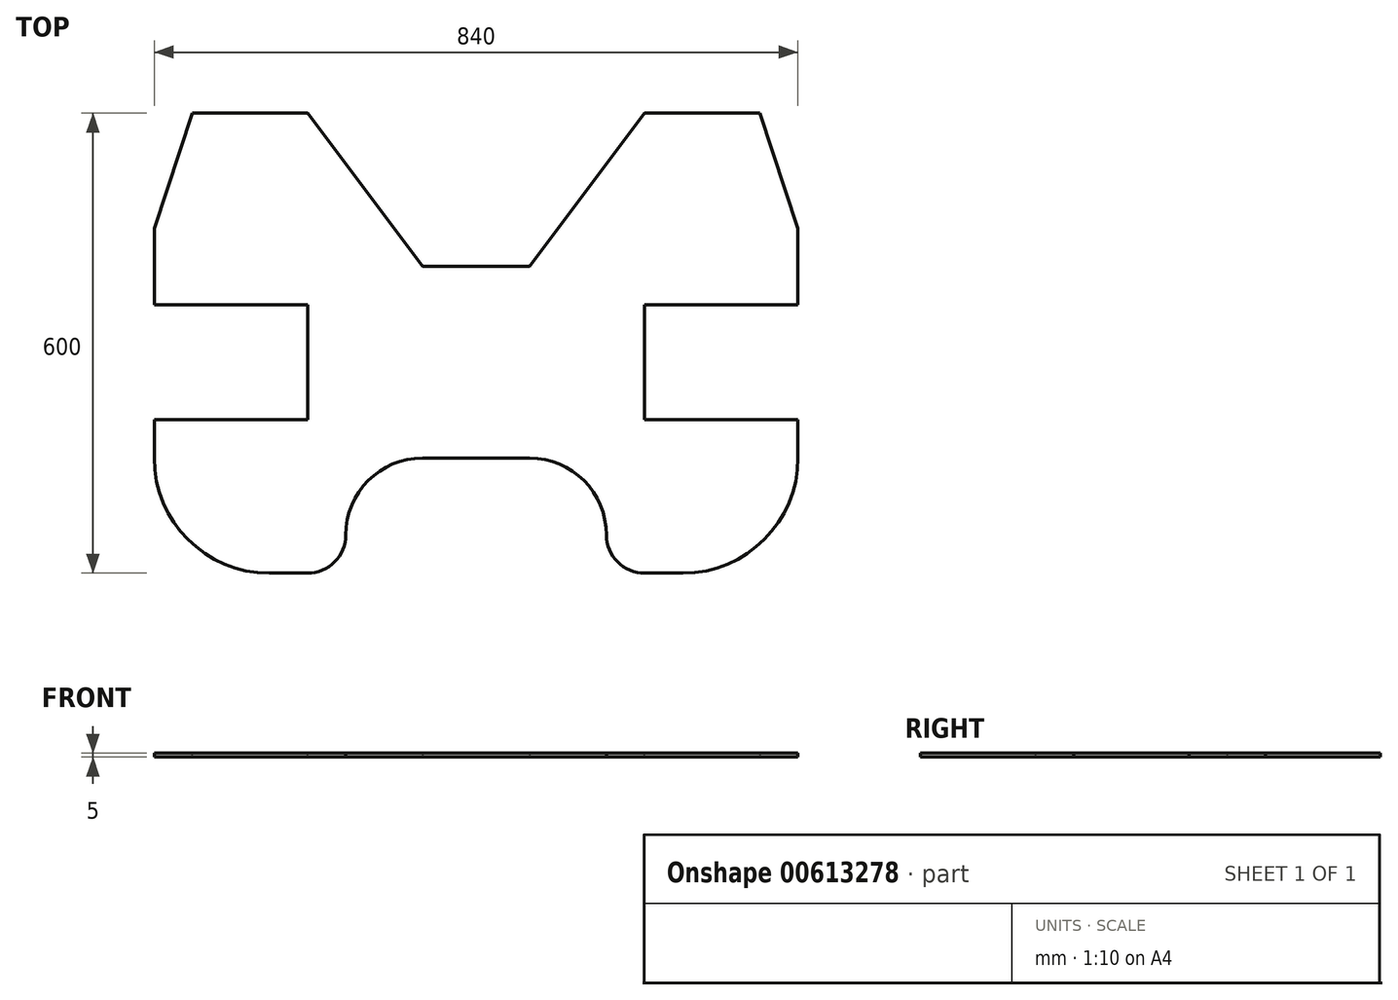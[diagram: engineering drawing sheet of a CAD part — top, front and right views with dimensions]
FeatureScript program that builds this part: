
annotation { "Feature Type Name" : "Feature", "Feature Type Description" : "" }
export const myFeature = defineFeature(function(context is Context, id is Id, definition is map)
    precondition{}
    {
        {
            var Q0;
            Q0=qCreatedBy(makeId("Top.planeOp"),FACE);
            var sketch = newSketch(context, id + "F0", { "sketchPlane" : qUnion([Q0])});
            skLineSegment(sketch, "E0.bottom", {"start": v(220, 125) * mm, "end": v(-220, 125) * mm});
            skLineSegment(sketch, "E0.top", {"start": v(220, -125) * mm, "end": v(-220, -125) * mm});
            skLineSegment(sketch, "E0.left", {"start": v(220, 125) * mm, "end": v(220, -125) * mm});
            skLineSegment(sketch, "E0.right", {"start": v(-220, 125) * mm, "end": v(-220, -125) * mm});
            skPoint(sketch, "E0.middle", {"position": v(0, 0) * mm});
            skSolve(sketch);
        }
        {
            var Q0;
            Q0 = qSketchRegion(id + "F0", true);
            extrude(context, id + "F1", {"entities" : qUnion([Q0]), "depth" : 5 * mm, "offsetDistance" : 25 * mm});
        }
        {
            var Q0;
            Q0=makeQuery(id+"F1.opExtrude","CAP_FACE",FACE,{"disambiguationData":[OSD([sQuery(id+"F0.wireOp",EDGE,"E0.bottom"),sQuery(id+"F0.wireOp",EDGE,"E0.top"),sQuery(id+"F0.wireOp",EDGE,"E0.left"),sQuery(id+"F0.wireOp",EDGE,"E0.right")])],"isStart":true});
            var sketch = newSketch(context, id + "F2", { "sketchPlane" : qUnion([Q0])});
            skLineSegment(sketch, "E1.bottom", {"start": v(-170, 75) * mm, "end": v(-420, 75) * mm});
            skLineSegment(sketch, "E1.top", {"start": v(-170, 275) * mm, "end": v(-420, 275) * mm});
            skLineSegment(sketch, "E1.left", {"start": v(-170, 75) * mm, "end": v(-170, 275) * mm});
            skLineSegment(sketch, "E1.right", {"start": v(-420, 75) * mm, "end": v(-420, 275) * mm});
            skLineSegment(sketch, "E2.bottom", {"start": v(170, 75) * mm, "end": v(420, 75) * mm});
            skLineSegment(sketch, "E2.top", {"start": v(170, 275) * mm, "end": v(420, 275) * mm});
            skLineSegment(sketch, "E2.left", {"start": v(170, 75) * mm, "end": v(170, 275) * mm});
            skLineSegment(sketch, "E2.right", {"start": v(420, 75) * mm, "end": v(420, 275) * mm});
            skLineSegment(sketch, "E3.bottom", {"start": v(-70, -75) * mm, "end": v(-420, -75) * mm});
            skLineSegment(sketch, "E3.top", {"start": v(-70, -325) * mm, "end": v(-420, -325) * mm});
            skLineSegment(sketch, "E3.left", {"start": v(-70, -75) * mm, "end": v(-70, -325) * mm});
            skLineSegment(sketch, "E3.right", {"start": v(-420, -75) * mm, "end": v(-420, -325) * mm});
            skLineSegment(sketch, "E4.bottom", {"start": v(70, -75) * mm, "end": v(420, -75) * mm});
            skLineSegment(sketch, "E4.top", {"start": v(70, -325) * mm, "end": v(420, -325) * mm});
            skLineSegment(sketch, "E4.left", {"start": v(70, -75) * mm, "end": v(70, -325) * mm});
            skLineSegment(sketch, "E4.right", {"start": v(420, -75) * mm, "end": v(420, -325) * mm});
            skSolve(sketch);
        }
        {
            var Q0;
            Q0 = qSketchRegion(id + "F2", true);
            extrude(context, id + "F3", {"entities" : qUnion([Q0]), "operationType" : NewBodyOperationType.ADD, "oppositeDirection" : true, "depth" : 5 * mm, "offsetDistance" : 25 * mm});
        }
        {
            var Q0;
            Q0=makeQuery(id+"F3.opExtrude","SWEPT_EDGE",EDGE,{"disambiguationData":[OSD([sQuery(id+"F2.wireOp",EDGE,"E1.top"),sQuery(id+"F2.wireOp",EDGE,"E1.right")])]});
            var Q1;
            Q1=makeQuery(id+"F3.opExtrude","SWEPT_EDGE",EDGE,{"disambiguationData":[OSD([sQuery(id+"F2.wireOp",EDGE,"E2.top"),sQuery(id+"F2.wireOp",EDGE,"E2.right")])]});
            fillet(context, id + "F4", {"entities" : qUnion([Q0, Q1]), "radius" : 150 * mm, "tangentPropagation" : true, "allowEdgeOverflow" : false});
        }
        {
            var Q0;
            Q0=makeQuery(id+"F3.boolean.opBoolean","INTERSECT",EDGE,{"derivedFrom":[makeQuery(id+"F1.opExtrude","SWEPT_FACE",FACE,{"disambiguationData":[OSD([sQuery(id+"F0.wireOp",EDGE,"E0.top")])]}),makeQuery(id+"F3.opExtrude","SWEPT_FACE",FACE,{"disambiguationData":[OSD([sQuery(id+"F2.wireOp",EDGE,"E2.left")])]})]});
            var Q1;
            Q1=makeQuery(id+"F3.boolean.opBoolean","INTERSECT",EDGE,{"derivedFrom":[makeQuery(id+"F1.opExtrude","SWEPT_FACE",FACE,{"disambiguationData":[OSD([sQuery(id+"F0.wireOp",EDGE,"E0.top")])]}),makeQuery(id+"F3.opExtrude","SWEPT_FACE",FACE,{"disambiguationData":[OSD([sQuery(id+"F2.wireOp",EDGE,"E1.left")])]})]});
            fillet(context, id + "F5", {"entities" : qUnion([Q0, Q1]), "radius" : 100 * mm, "tangentPropagation" : true, "allowEdgeOverflow" : false});
        }
        {
            var Q0;
            Q0=makeQuery(id+"F3.opExtrude","SWEPT_EDGE",EDGE,{"disambiguationData":[OSD([sQuery(id+"F2.wireOp",EDGE,"E1.top"),sQuery(id+"F2.wireOp",EDGE,"E1.left")])]});
            var Q1;
            Q1=makeQuery(id+"F3.opExtrude","SWEPT_EDGE",EDGE,{"disambiguationData":[OSD([sQuery(id+"F2.wireOp",EDGE,"E2.top"),sQuery(id+"F2.wireOp",EDGE,"E2.left")])]});
            fillet(context, id + "F6", {"entities" : qUnion([Q0, Q1]), "radius" : 50 * mm, "tangentPropagation" : true, "allowEdgeOverflow" : false});
        }
        {
            var Q0;
            Q0=makeQuery(id+"F3.opExtrude","SWEPT_EDGE",EDGE,{"disambiguationData":[OSD([sQuery(id+"F2.wireOp",EDGE,"E4.top"),sQuery(id+"F2.wireOp",EDGE,"E4.right")])]});
            chamfer(context, id + "F7", {"entities" : qUnion([Q0]), "chamferType" : ChamferType.TWO_OFFSETS, "width1" : 50 * mm, "oppositeDirection" : false, "width2" : 150 * mm, "tangentPropagation" : true});
        }
        {
            var Q0;
            Q0=makeQuery(id+"F3.opExtrude","SWEPT_EDGE",EDGE,{"disambiguationData":[OSD([sQuery(id+"F2.wireOp",EDGE,"E3.top"),sQuery(id+"F2.wireOp",EDGE,"E3.right")])]});
            chamfer(context, id + "F8", {"entities" : qUnion([Q0]), "chamferType" : ChamferType.TWO_OFFSETS, "width1" : 150 * mm, "oppositeDirection" : false, "width2" : 50 * mm, "tangentPropagation" : true});
        }
        {
            var Q0;
            Q0=makeQuery(id+"F3.boolean.opBoolean","MERGE",FACE,{"derivedFrom":[makeQuery(id+"F1.opExtrude","CAP_FACE",FACE,{"disambiguationData":[OSD([sQuery(id+"F0.wireOp",EDGE,"E0.bottom"),sQuery(id+"F0.wireOp",EDGE,"E0.top"),sQuery(id+"F0.wireOp",EDGE,"E0.left"),sQuery(id+"F0.wireOp",EDGE,"E0.right")])],"isStart":false}),makeQuery(id+"F3.opExtrude","CAP_FACE",FACE,{"disambiguationData":[OSD([sQuery(id+"F2.wireOp",EDGE,"E1.bottom"),sQuery(id+"F2.wireOp",EDGE,"E1.top"),sQuery(id+"F2.wireOp",EDGE,"E1.left"),sQuery(id+"F2.wireOp",EDGE,"E1.right")])],"isStart":false}),makeQuery(id+"F3.opExtrude","CAP_FACE",FACE,{"disambiguationData":[OSD([sQuery(id+"F2.wireOp",EDGE,"E2.bottom"),sQuery(id+"F2.wireOp",EDGE,"E2.top"),sQuery(id+"F2.wireOp",EDGE,"E2.left"),sQuery(id+"F2.wireOp",EDGE,"E2.right")])],"isStart":false}),makeQuery(id+"F3.opExtrude","CAP_FACE",FACE,{"disambiguationData":[OSD([sQuery(id+"F2.wireOp",EDGE,"E3.bottom"),sQuery(id+"F2.wireOp",EDGE,"E3.top"),sQuery(id+"F2.wireOp",EDGE,"E3.left"),sQuery(id+"F2.wireOp",EDGE,"E3.right")])],"isStart":false}),makeQuery(id+"F3.opExtrude","CAP_FACE",FACE,{"disambiguationData":[OSD([sQuery(id+"F2.wireOp",EDGE,"E4.bottom"),sQuery(id+"F2.wireOp",EDGE,"E4.top"),sQuery(id+"F2.wireOp",EDGE,"E4.left"),sQuery(id+"F2.wireOp",EDGE,"E4.right")])],"isStart":false})]});
            var sketch = newSketch(context, id + "F9", { "sketchPlane" : qUnion([Q0])});
            skLineSegment(sketch, "E5", {"start": v(-70, 125) * mm, "end": v(-220, 325) * mm});
            skLineSegment(sketch, "E6", {"start": v(-220, 325) * mm, "end": v(-70, 325) * mm});
            skLineSegment(sketch, "E7", {"start": v(-70, 325) * mm, "end": v(-70, 125) * mm});
            skLineSegment(sketch, "E8", {"start": v(70, 125) * mm, "end": v(220, 325) * mm});
            skLineSegment(sketch, "E9", {"start": v(220, 325) * mm, "end": v(70, 325) * mm});
            skLineSegment(sketch, "E10", {"start": v(70, 325) * mm, "end": v(70, 125) * mm});
            skSolve(sketch);
        }
        {
            var Q0;
            Q0 = qSketchRegion(id + "F9", true);
            extrude(context, id + "F10", {"entities" : qUnion([Q0]), "operationType" : NewBodyOperationType.REMOVE, "oppositeDirection" : true, "depth" : 25 * mm, "offsetDistance" : 25 * mm});
        }
    });
